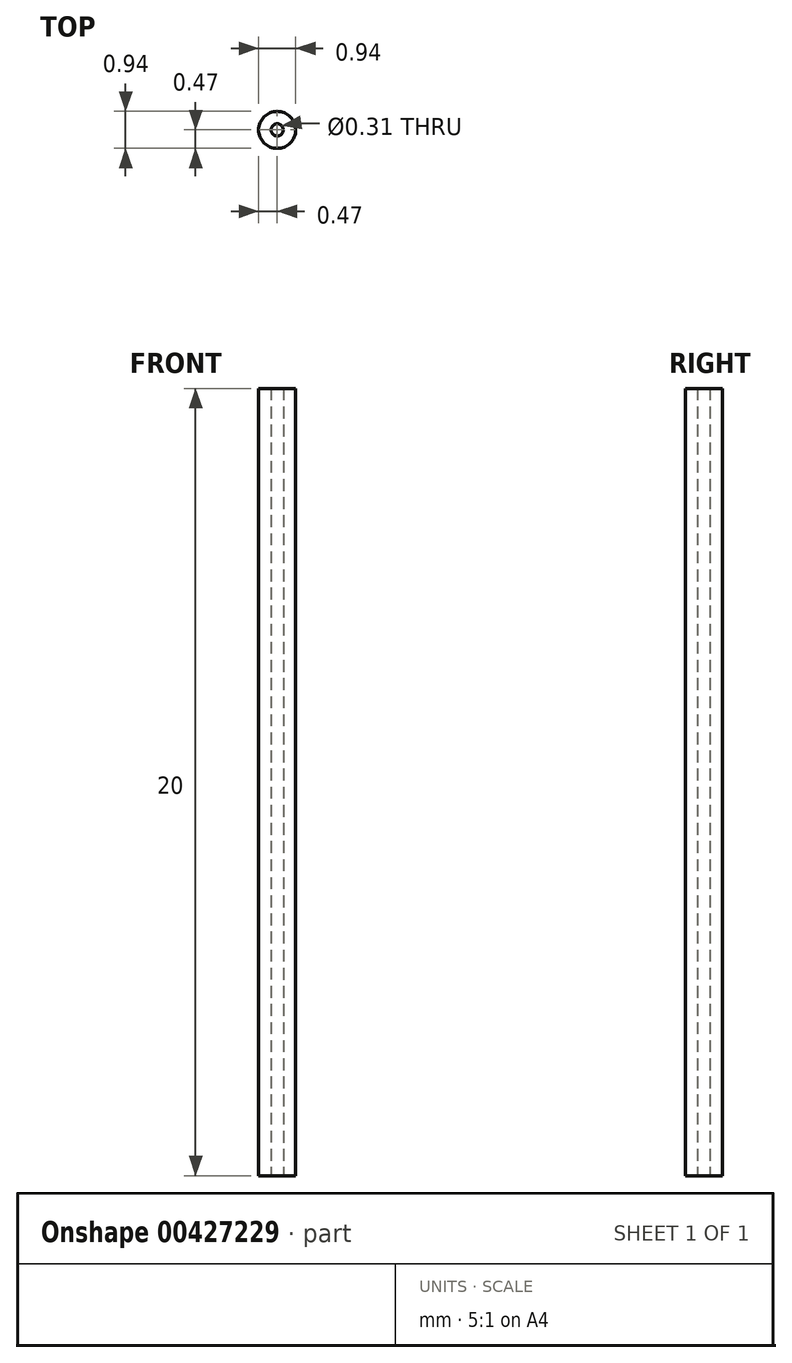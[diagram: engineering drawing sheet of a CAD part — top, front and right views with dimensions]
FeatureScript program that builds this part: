
annotation { "Feature Type Name" : "Feature", "Feature Type Description" : "" }
export const myFeature = defineFeature(function(context is Context, id is Id, definition is map)
    precondition{}
    {
        {
            var Q0;
            Q0=qCreatedBy(makeId("Top.planeOp"),FACE);
            var sketch = newSketch(context, id + "F0", { "sketchPlane" : qUnion([Q0])});
            skCircle(sketch, "E0", {"center": v(0, 0) * mm, "radius": 0.47 * mm});
            skCircle(sketch, "E1", {"center": v(0, 0) * mm, "radius": 0.16 * mm});
            skSolve(sketch);
        }
        {
            var Q0;
            Q0=makeQuery(id+"F0.imprint","IMPRINT",FACE,{"disambiguationData":[TD([[makeQuery(id+"F0.imprint","IMPRINT",EDGE,{"derivedFrom":sQuery(id+"F0.wireOp",EDGE,"E0")}),1.0]])]});
            extrude(context, id + "F1", {"entities" : qUnion([Q0]), "depth" : 20 * mm});
        }
    });
